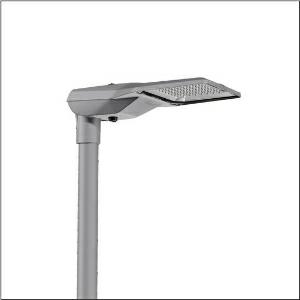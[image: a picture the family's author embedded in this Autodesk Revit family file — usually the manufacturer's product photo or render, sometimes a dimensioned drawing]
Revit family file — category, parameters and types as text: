
# Revit family: streetlight_sl_21_iq_midi___st1_0a_5xe3d61y08mb_8671
name_source: partatom
category: Lighting Fixtures
units: mm (PartAtom-declared; Revit-internal decimal feet)

## family parameters
Cut with Voids When Loaded = No
Host = Face
Light Source = No
Part Type = Normal
Room Calculation Point = No
Round Connector Dimension = Use Diameter
Shared = No

## types (1)
- --- (1 x LED, 15910 lm, 129.3 W, 2700K)
    Apparent Load = 129 VA
    CIE Flux Codes = 37 72 97 100 100
    Color Rendering = 70
    Color Temperature = 2700K
    Default Elevation = 1800 mm
    Description = Streetlight SL 21 iQ midi, mast luminaire, primary light control with lens, of PMMA, primary optical cover: cover, of toughened safety glass, transparent, light distribution: ST1.0a, light emission: direct distribution, primary light characteristic: asymmetric, installation type: post-top, side-entry, LED, High Power LED, rated luminous flux: 15.910lm, luminous efficacy: 123lm/W, light colour: 727, colour temperature: 2700K, control gear: iQ-Street Remote, D4i with power reduction, control: pre-setting: logarithmic dimming characteristic, Street-Remote, Auto-Match, Temp-Guard, Lumen-Switch, Night-Set, Smart-Wire, Light-Fading, Desk-Remote (wireless, voltage-free reading and setting of iQ features in the workshop via application-optimized NFC function/RFID function), optimised constant luminous flux control (CLO 2.0), mains connection: 230..240V, AC, 50/60Hz, start of lifetime: 129W, end of service life: 142W, reduction: 56W, luminaire housing, of diecast aluminium, powder-coated, Siteco® metallic grey (DB 702S), corrosivity category C5 mid according to DIN EN ISO 12944, please order mast flange separately, inclination adjustable: 0°, 5°, 10°, 15°, sealing non-destructively replaceable, multi-level sealing system, length: 644mm, width: 335mm, height: 110mm, mast flange for spigot size: 42mm (side-entry): 5XC10008XM4, 60/48mm (side-entry/post-top): 5XC10108XM2, 76/60mm (side-entry/post-top): 5XC10108XM1, mounting height: 4..8m, Smart Interface below and above, protection rating (complete): IP66, insulation class (complete): insulation class II (safety insulation), certification: CE, ENEC, ENEC+, VDE, impact resistance: IK10, permissible operating ambient temperature for outdoor applications: -40..+50°C, standard-compliant lighting for roads and squares, packaging unit: 1 piece

Light Distribution: ST1.0a
    Height = 111 mm
    Lamp = 1 x LED
    Lamp Light Flux = 15910 lm
    Lamp Power = 129.3 W
    Lamp count = 1
    Length = 644 mm
    Luminous efficacy = 123 lm/W
    Manufacturer = Siteco
    ModVariant = No
    Model = 5XE3D61Y08MB
    Number of Poles = 1
    OnlyDefault = Yes
    Power Factor = 1
    Product Name = Streetlight SL 21 iQ midi | ST1.0a
    Product group = mast luminaire | pylon top
    ProductGroupID = 6100
    Protection Class = Protection class II
    Protection Degree = IP 66
    RLX_Detail_Level = 1
    RLX_Emergency_Light_Flux = 0 lm
    RLX_Emergency_Type = 0
    RLX_Emergency_Type_DB = No
    RlxData = <blob elided: 91037 chars, md5=04ca6514>
    Socket = socket
    Standby Power = 0 W
    System Light Flux = 15910 lm
    System Power = 129 W
    Type Comments = factory setting: luminous flux: 100 % | dim-lin: 254 | 672 mA
    Type Image = l_1004304.jpg
    URL = http://relux.com
    VarID = @adj_136045
    Voltage = 0 V
    Weight = 0.00 kg
    Width = 336 mm

## geometry (parser evidence)
native form markers: Blend x4, Sweep x10
no freeform markers — native parametric forms only
